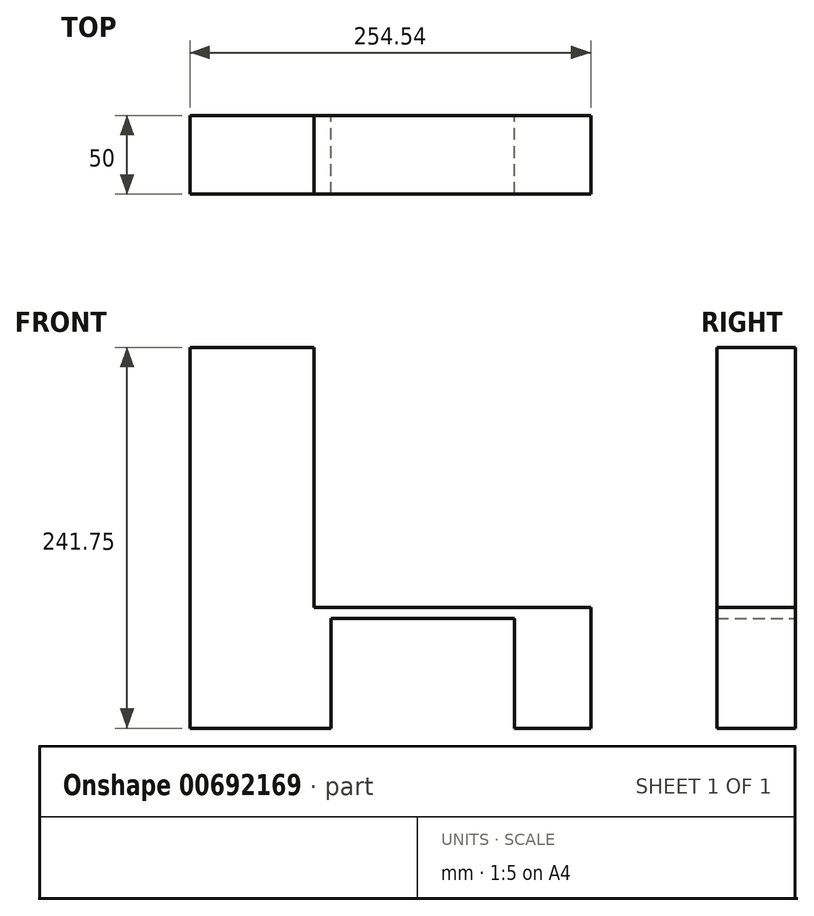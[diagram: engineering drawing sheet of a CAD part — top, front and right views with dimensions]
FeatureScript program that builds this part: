
annotation { "Feature Type Name" : "Feature", "Feature Type Description" : "" }
export const myFeature = defineFeature(function(context is Context, id is Id, definition is map)
    precondition{}
    {
        {
            var Q0;
            Q0=qCreatedBy(makeId("Front.planeOp"),FACE);
            var sketch = newSketch(context, id + "F0", { "sketchPlane" : qUnion([Q0])});
            skLineSegment(sketch, "E0", {"start": v(-93.51, -64.3) * mm, "end": v(162.22, -64.3) * mm});
            skLineSegment(sketch, "E1", {"start": v(162.22, -64.3) * mm, "end": v(162.22, 151.2) * mm});
            skLineSegment(sketch, "E2", {"start": v(-93.51, -64.3) * mm, "end": v(-93.51, 190.75) * mm});
            skLineSegment(sketch, "E3", {"start": v(-93.51, 190.75) * mm, "end": v(162.22, 151.2) * mm});
            skSolve(sketch);
        }
        {
            var Q0;
            Q0=makeQuery(id+"F0.imprint","IMPRINT",FACE,{"disambiguationData":[TD([[makeQuery(id+"F0.imprint","IMPRINT",EDGE,{"derivedFrom":sQuery(id+"F0.wireOp",EDGE,"E0")}),1.0]])]});
            var sketch = newSketch(context, id + "F1", { "sketchPlane" : qUnion([Q0])});
            skLineSegment(sketch, "E4.bottom", {"start": v(-94.25, -63.8) * mm, "end": v(-74.01, -63.8) * mm});
            skLineSegment(sketch, "E4.top", {"start": v(-94.25, 107.13) * mm, "end": v(-74.01, 107.13) * mm});
            skLineSegment(sketch, "E4.left", {"start": v(-94.25, -63.8) * mm, "end": v(-94.25, 107.13) * mm});
            skLineSegment(sketch, "E4.right", {"start": v(-74.01, -63.8) * mm, "end": v(-74.01, 107.13) * mm});
            skLineSegment(sketch, "E5.bottom", {"start": v(-74.01, 107.13) * mm, "end": v(-15.43, 107.13) * mm});
            skLineSegment(sketch, "E5.top", {"start": v(-74.01, 107.13) * mm, "end": v(-15.43, 107.13) * mm});
            skLineSegment(sketch, "E5.left", {"start": v(-74.01, 107.13) * mm, "end": v(-74.01, 107.13) * mm});
            skLineSegment(sketch, "E5.right", {"start": v(-15.43, 107.13) * mm, "end": v(-15.43, 107.13) * mm});
            skLineSegment(sketch, "E6.bottom", {"start": v(-15.43, 107.13) * mm, "end": v(-74.01, 107.13) * mm});
            skLineSegment(sketch, "E6.top", {"start": v(-15.43, -63.8) * mm, "end": v(-74.01, -63.8) * mm});
            skLineSegment(sketch, "E6.left", {"start": v(-15.43, 107.13) * mm, "end": v(-15.43, -63.8) * mm});
            skLineSegment(sketch, "E6.right", {"start": v(-74.01, 107.13) * mm, "end": v(-74.01, -63.8) * mm});
            skLineSegment(sketch, "E7.bottom", {"start": v(-15.43, -63.8) * mm, "end": v(-4.78, -63.8) * mm});
            skLineSegment(sketch, "E7.top", {"start": v(-15.43, 5.95) * mm, "end": v(-4.78, 5.95) * mm});
            skLineSegment(sketch, "E7.left", {"start": v(-15.43, -63.8) * mm, "end": v(-15.43, 5.95) * mm});
            skLineSegment(sketch, "E7.right", {"start": v(-4.78, -63.8) * mm, "end": v(-4.78, 5.95) * mm});
            skLineSegment(sketch, "E8", {"start": v(-4.78, 5.95) * mm, "end": v(160.3, 5.95) * mm});
            skLineSegment(sketch, "E9.bottom", {"start": v(160.3, 5.95) * mm, "end": v(149.64, 5.95) * mm});
            skLineSegment(sketch, "E9.top", {"start": v(160.3, -63.8) * mm, "end": v(149.64, -63.8) * mm});
            skLineSegment(sketch, "E9.left", {"start": v(160.3, 5.95) * mm, "end": v(160.3, -63.8) * mm});
            skLineSegment(sketch, "E9.right", {"start": v(149.64, 5.95) * mm, "end": v(149.64, -63.8) * mm});
            skLineSegment(sketch, "E10.bottom", {"start": v(-15.43, 5.95) * mm, "end": v(160.3, 5.95) * mm});
            skLineSegment(sketch, "E10.top", {"start": v(-15.43, 12.88) * mm, "end": v(160.3, 12.88) * mm});
            skLineSegment(sketch, "E10.left", {"start": v(-15.43, 5.95) * mm, "end": v(-15.43, 12.88) * mm});
            skLineSegment(sketch, "E10.right", {"start": v(160.3, 5.95) * mm, "end": v(160.3, 12.88) * mm});
            skLineSegment(sketch, "E11.bottom", {"start": v(160.3, 5.95) * mm, "end": v(111.83, 5.95) * mm});
            skLineSegment(sketch, "E11.top", {"start": v(160.3, -63.8) * mm, "end": v(111.83, -63.8) * mm});
            skLineSegment(sketch, "E11.right", {"start": v(111.83, 5.95) * mm, "end": v(111.83, -63.8) * mm});
            skLineSegment(sketch, "E12.bottom", {"start": v(-15.43, 107.13) * mm, "end": v(-94.25, 107.13) * mm});
            skLineSegment(sketch, "E12.top", {"start": v(-15.43, 177.95) * mm, "end": v(-94.25, 177.95) * mm});
            skLineSegment(sketch, "E12.left", {"start": v(-15.43, 107.13) * mm, "end": v(-15.43, 177.95) * mm});
            skLineSegment(sketch, "E12.right", {"start": v(-94.25, 107.13) * mm, "end": v(-94.25, 177.95) * mm});
            skSolve(sketch);
        }
        {
            var Q0;
            Q0 = qSketchRegion(id + "F1", true);
            extrude(context, id + "F2", {"entities" : qUnion([Q0]), "depth" : 50 * mm, "offsetDistance" : 25 * mm});
        }
    });
